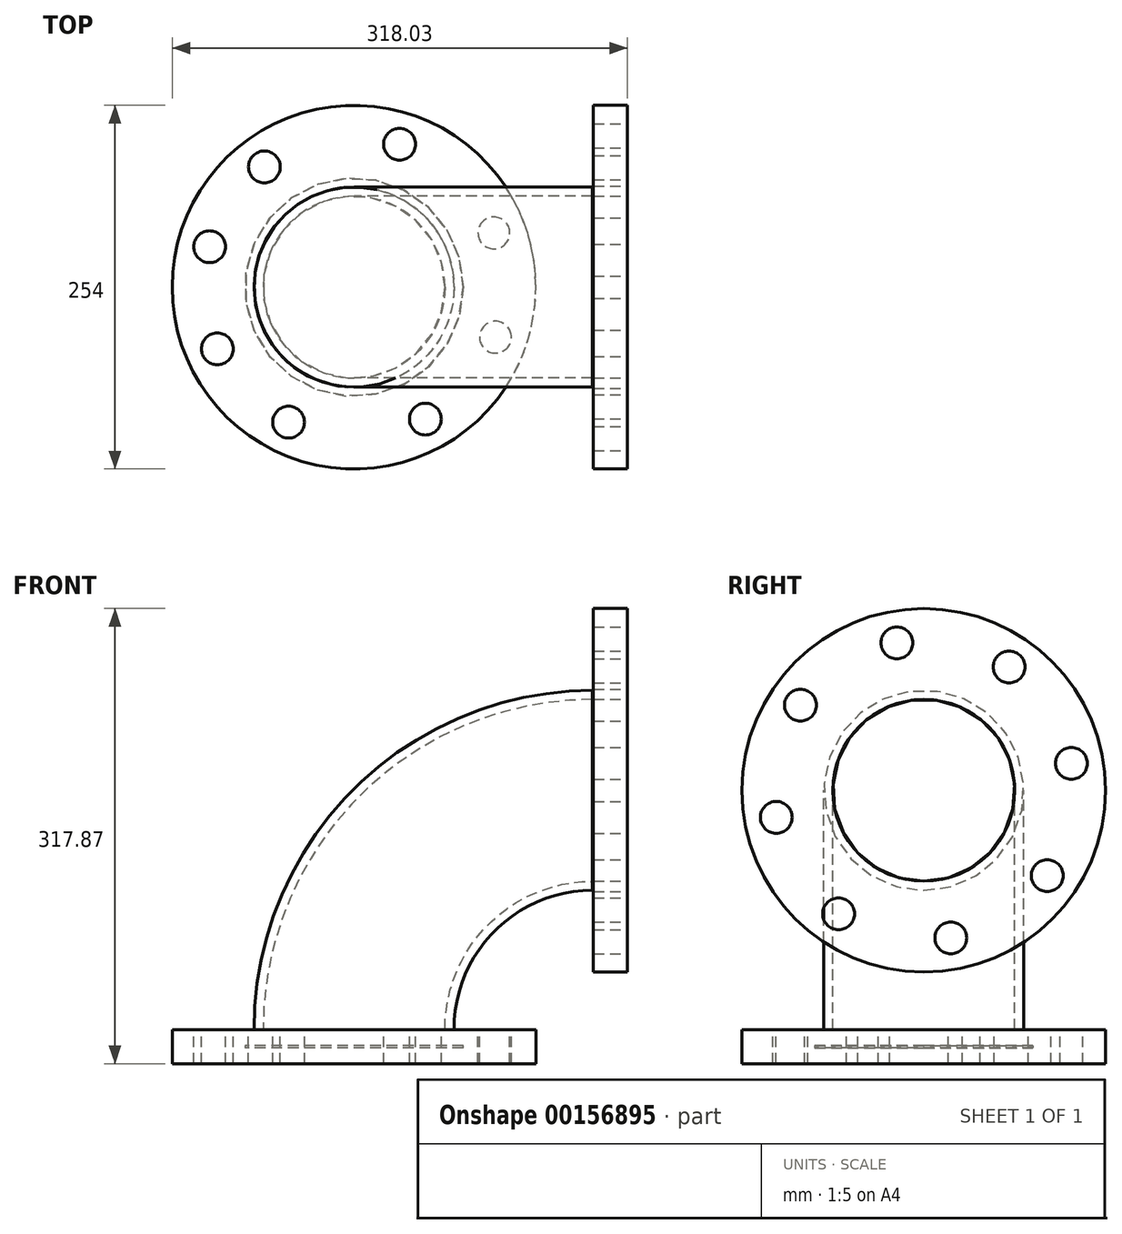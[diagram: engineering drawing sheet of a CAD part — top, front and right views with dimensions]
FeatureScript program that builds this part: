
annotation { "Feature Type Name" : "Feature", "Feature Type Description" : "" }
export const myFeature = defineFeature(function(context is Context, id is Id, definition is map)
    precondition{}
    {
        {
            var Q0;
            Q0=qCreatedBy(makeId("Front.planeOp"),FACE);
            var sketch = newSketch(context, id + "F0", { "sketchPlane" : qUnion([Q0])});
            skLineSegment(sketch, "E0.bottom", {"start": v(0, 0) * mm, "end": v(127, 0) * mm});
            skLineSegment(sketch, "E0.top", {"start": v(0, 23.81) * mm, "end": v(127, 23.81) * mm});
            skLineSegment(sketch, "E0.left", {"start": v(0, 0) * mm, "end": v(0, 23.81) * mm});
            skLineSegment(sketch, "E0.right", {"start": v(127, 0) * mm, "end": v(127, 23.81) * mm});
            skPoint(sketch, "E1.endSnap0", {"position": v(0, 11.9) * mm});
            skLineSegment(sketch, "E2.bottom", {"start": v(191.03, 190.87) * mm, "end": v(167.22, 190.87) * mm});
            skLineSegment(sketch, "E2.top", {"start": v(191.03, 63.87) * mm, "end": v(167.22, 63.87) * mm});
            skLineSegment(sketch, "E2.left", {"start": v(191.03, 190.87) * mm, "end": v(191.03, 63.87) * mm});
            skLineSegment(sketch, "E2.right", {"start": v(167.22, 190.87) * mm, "end": v(167.22, 63.87) * mm});
            skLineSegment(sketch, "E3", {"start": v(0, 23.81) * mm, "end": v(0, 24.18) * mm});
            skLineSegment(sketch, "E4", {"start": v(166.69, 190.87) * mm, "end": v(167.22, 190.87) * mm});
            skPoint(sketch, "E5.visualSharp", {"position": v(0, 190.87) * mm});
            skArc(sketch, "E5.filletArc", {"start": v(166.69, 190.87) * mm, "mid": v(48.82, 142.05) * mm, "end": v(0, 24.18) * mm, "construction": true});
            skLineSegment(sketch, "E6", {"start": v(0, 0) * mm, "end": v(0, 24.18) * mm, "construction": true});
            skLineSegment(sketch, "E7", {"start": v(191.03, 190.87) * mm, "end": v(167.22, 190.87) * mm, "construction": true});
            skLineSegment(sketch, "E8", {"start": v(0, 24.18) * mm, "end": v(63.5, 23.81) * mm});
            skLineSegment(sketch, "E9", {"start": v(167.22, 190.87) * mm, "end": v(167.22, 127.37) * mm});
            skLineSegment(sketch, "E10", {"start": v(63.5, 23.81) * mm, "end": v(63.5, 24.18) * mm});
            skLineSegment(sketch, "E11", {"start": v(166.69, 127.37) * mm, "end": v(167.22, 127.37) * mm});
            skPoint(sketch, "E12.visualSharp", {"position": v(63.5, 127.37) * mm});
            skArc(sketch, "E12.filletArc", {"start": v(166.69, 127.37) * mm, "mid": v(93.72, 97.15) * mm, "end": v(63.5, 24.18) * mm});
            skLineSegment(sketch, "E13", {"start": v(0, 24.18) * mm, "end": v(0, 24.18) * mm});
            skLineSegment(sketch, "E14", {"start": v(167.22, 190.87) * mm, "end": v(166.69, 190.87) * mm});
            skArc(sketch, "E15.filletArc", {"start": v(166.69, 190.87) * mm, "mid": v(48.82, 142.05) * mm, "end": v(0, 24.18) * mm});
            skLineSegment(sketch, "E16", {"start": v(0, -20.98) * mm, "end": v(0, 78.24) * mm, "construction": true});
            skLineSegment(sketch, "E17", {"start": v(208.52, 190.87) * mm, "end": v(129.26, 190.87) * mm, "construction": true});
            skSolve(sketch);
        }
        {
            var Q0;
            Q0=makeQuery(id+"F0.imprint","IMPRINT",FACE,{"disambiguationData":[TD([[makeQuery(id+"F0.imprint","IMPRINT",EDGE,{"derivedFrom":sQuery(id+"F0.wireOp",EDGE,"E2.bottom")}),1.0]])]});
            var Q1;
            Q1=sQuery(id+"F0.wireOp",EDGE,"E17");
            revolve(context, id + "F1", {"entities" : qUnion([Q0]), "axis" : qUnion([Q1]), "revolveType" : RevolveType.FULL});
        }
        {
            var Q0;
            Q0=makeQuery(id+"F0.imprint","IMPRINT",FACE,{"disambiguationData":[TD([[makeQuery(id+"F0.imprint","IMPRINT",EDGE,{"derivedFrom":sQuery(id+"F0.wireOp",EDGE,"E0.bottom")}),1.0]])]});
            var Q1;
            Q1=sQuery(id+"F0.wireOp",EDGE,"E16");
            revolve(context, id + "F2", {"entities" : qUnion([Q0]), "axis" : qUnion([Q1]), "revolveType" : RevolveType.FULL});
        }
        {
            var Q0;
            Q0=makeQuery(id+"F2.opRevolve","SWEPT_FACE",FACE,{"disambiguationData":[OSD([sQuery(id+"F0.wireOp",EDGE,"E0.top")])]});
            var sketch = newSketch(context, id + "F3", { "sketchPlane" : qUnion([Q0])});
            skCircle(sketch, "E18", {"center": v(0, 0) * mm, "radius": 63.5 * mm});
            skCircle(sketch, "E19", {"center": v(0, 0) * mm, "radius": 69.85 * mm});
            skCircle(sketch, "E20", {"center": v(0, 0) * mm, "radius": 104.78 * mm});
            skCircle(sketch, "E21", {"center": v(-95.5, -43.1) * mm, "radius": 11.11 * mm});
            skCircle(sketch, "E22", {"center": v(-45.7, -94.28) * mm, "radius": 11.11 * mm});
            skCircle(sketch, "E23", {"center": v(-100.9, 28.26) * mm, "radius": 11.11 * mm});
            skCircle(sketch, "E24", {"center": v(-62.62, 84) * mm, "radius": 11.11 * mm});
            skCircle(sketch, "E25", {"center": v(31.8, 99.84) * mm, "radius": 11.11 * mm});
            skCircle(sketch, "E26", {"center": v(97.7, 37.87) * mm, "radius": 11.11 * mm});
            skCircle(sketch, "E27", {"center": v(98.79, -34.91) * mm, "radius": 11.11 * mm});
            skCircle(sketch, "E28", {"center": v(49.84, -92.16) * mm, "radius": 11.11 * mm});
            skSolve(sketch);
        }
        {
            var Q0;
            Q0=makeQuery(id+"F3.imprint","IMPRINT",FACE,{"disambiguationData":[TD([[makeQuery(id+"F3.imprint","IMPRINT",EDGE,{"derivedFrom":sQuery(id+"F3.wireOp",EDGE,"E18")}),-1.0]])]});
            var Q1;
            Q1=sQuery(id+"F0.wireOp",EDGE,"E15.filletArc");
            sweep(context, id + "F4", {"operationType" : NewBodyOperationType.ADD, "profiles" : qUnion([Q0]), "path" : qUnion([Q1])});
        }
        {
            var Q0;
            Q0=sQuery(id+"F3.wireOp",VERTEX,"E21.center");
            var Q1;
            Q1=makeQuery(id+"F2.opRevolve","SWEPT_BODY",BODY,{"disambiguationData":[OSD([sQuery(id+"F0.wireOp",EDGE,"E0.bottom"),sQuery(id+"F0.wireOp",EDGE,"E0.top"),sQuery(id+"F0.wireOp",EDGE,"E0.left"),sQuery(id+"F0.wireOp",EDGE,"E0.right")])]});
            hole(context, id + "F5", {"style" : HoleStyle.SIMPLE, "endStyle" : HoleEndStyle.THROUGH, "holeDiameter" : 22.22 * mm, "locations" : qUnion([Q0]), "scope" : qUnion([Q1]), "isTappedThrough" : true});
        }
        {
            var Q0;
            Q0=sQuery(id+"F3.wireOp",VERTEX,"E22.center");
            var Q1;
            Q1=makeQuery(id+"F2.opRevolve","SWEPT_BODY",BODY,{"disambiguationData":[OSD([sQuery(id+"F0.wireOp",EDGE,"E0.bottom"),sQuery(id+"F0.wireOp",EDGE,"E0.top"),sQuery(id+"F0.wireOp",EDGE,"E0.left"),sQuery(id+"F0.wireOp",EDGE,"E0.right")])]});
            hole(context, id + "F6", {"style" : HoleStyle.SIMPLE, "endStyle" : HoleEndStyle.THROUGH, "holeDiameter" : 22.22 * mm, "locations" : qUnion([Q0]), "scope" : qUnion([Q1]), "isTappedThrough" : true});
        }
        {
            var Q0;
            Q0=sQuery(id+"F3.wireOp",VERTEX,"E23.center");
            var Q1;
            Q1=makeQuery(id+"F2.opRevolve","SWEPT_BODY",BODY,{"disambiguationData":[OSD([sQuery(id+"F0.wireOp",EDGE,"E0.bottom"),sQuery(id+"F0.wireOp",EDGE,"E0.top"),sQuery(id+"F0.wireOp",EDGE,"E0.left"),sQuery(id+"F0.wireOp",EDGE,"E0.right")])]});
            hole(context, id + "F7", {"style" : HoleStyle.SIMPLE, "endStyle" : HoleEndStyle.THROUGH, "holeDiameter" : 22.22 * mm, "locations" : qUnion([Q0]), "scope" : qUnion([Q1]), "isTappedThrough" : true});
        }
        {
            var Q0;
            Q0=sQuery(id+"F3.wireOp",VERTEX,"E24.center");
            var Q1;
            Q1=sQuery(id+"F3.wireOp",VERTEX,"E25.center");
            var Q2;
            Q2=sQuery(id+"F3.wireOp",VERTEX,"E26.center");
            var Q3;
            Q3=sQuery(id+"F3.wireOp",VERTEX,"E27.center");
            var Q4;
            Q4=sQuery(id+"F3.wireOp",VERTEX,"E28.center");
            var Q5;
            Q5=makeQuery(id+"F2.opRevolve","SWEPT_BODY",BODY,{"disambiguationData":[OSD([sQuery(id+"F0.wireOp",EDGE,"E0.bottom"),sQuery(id+"F0.wireOp",EDGE,"E0.top"),sQuery(id+"F0.wireOp",EDGE,"E0.left"),sQuery(id+"F0.wireOp",EDGE,"E0.right")])]});
            hole(context, id + "F8", {"style" : HoleStyle.SIMPLE, "endStyle" : HoleEndStyle.THROUGH, "holeDiameter" : 22.22 * mm, "locations" : qUnion([Q0, Q1, Q2, Q3, Q4]), "scope" : qUnion([Q5]), "isTappedThrough" : true});
        }
        {
            var Q0;
            Q0=makeQuery(id+"F1.opRevolve","SWEPT_FACE",FACE,{"disambiguationData":[OSD([sQuery(id+"F0.wireOp",EDGE,"E2.left")])]});
            var sketch = newSketch(context, id + "F9", { "sketchPlane" : qUnion([Q0])});
            skCircle(sketch, "E29", {"center": v(0, 190.87) * mm, "radius": 104.77 * mm, "construction": true});
            skCircle(sketch, "E30", {"center": v(-59.55, 104.66) * mm, "radius": 11.11 * mm});
            skLineSegment(sketch, "E31.anchor1", {"start": v(0, 190.87) * mm, "end": v(-59.55, 104.66) * mm, "construction": true});
            skLineSegment(sketch, "E31.anchor2", {"start": v(0, 190.87) * mm, "end": v(-59.55, 104.66) * mm, "construction": true});
            skCircle(sketch, "E32.1.0", {"center": v(18.85, 87.8) * mm, "radius": 11.11 * mm});
            skCircle(sketch, "E32.2.0", {"center": v(86.2, 131.32) * mm, "radius": 11.11 * mm});
            skCircle(sketch, "E33.1.3.0", {"center": v(103.07, 209.72) * mm, "radius": 11.11 * mm});
            skCircle(sketch, "E33.1.4.0", {"center": v(59.55, 277.08) * mm, "radius": 11.11 * mm});
            skCircle(sketch, "E33.1.5.0", {"center": v(-18.85, 293.93) * mm, "radius": 11.11 * mm});
            skCircle(sketch, "E33.1.6.0", {"center": v(-86.2, 250.42) * mm, "radius": 11.11 * mm});
            skCircle(sketch, "E33.1.7.0", {"center": v(-103.07, 172.02) * mm, "radius": 11.11 * mm});
            skSolve(sketch);
        }
        {
            var Q0;
            Q0=sQuery(id+"F9.wireOp",VERTEX,"E31.anchor1.end");
            var Q1;
            Q1=sQuery(id+"F9.wireOp",VERTEX,"E33.1.7.0.center");
            var Q2;
            Q2=sQuery(id+"F9.wireOp",VERTEX,"E33.1.6.0.center");
            var Q3;
            Q3=sQuery(id+"F9.wireOp",VERTEX,"E33.1.5.0.center");
            var Q4;
            Q4=sQuery(id+"F9.wireOp",VERTEX,"E33.1.4.0.center");
            var Q5;
            Q5=sQuery(id+"F9.wireOp",VERTEX,"E33.1.3.0.center");
            var Q6;
            Q6=sQuery(id+"F9.wireOp",VERTEX,"E32.2.0.center");
            var Q7;
            Q7=sQuery(id+"F9.wireOp",VERTEX,"E32.1.0.center");
            var Q8;
            Q8=makeQuery(id+"F1.opRevolve","SWEPT_BODY",BODY,{"disambiguationData":[OSD([sQuery(id+"F0.wireOp",EDGE,"E2.bottom"),sQuery(id+"F0.wireOp",EDGE,"E2.top"),sQuery(id+"F0.wireOp",EDGE,"E2.left"),sQuery(id+"F0.wireOp",EDGE,"E2.right"),sQuery(id+"F0.wireOp",EDGE,"E9")])]});
            hole(context, id + "F10", {"style" : HoleStyle.SIMPLE, "endStyle" : HoleEndStyle.THROUGH, "holeDiameter" : 22.22 * mm, "locations" : qUnion([Q0, Q1, Q2, Q3, Q4, Q5, Q6, Q7]), "scope" : qUnion([Q8]), "isTappedThrough" : true});
        }
        {
            var Q0;
            Q0=sQuery(id+"F9.wireOp",VERTEX,"E29.center");
            var Q1;
            Q1=makeQuery(id+"F1.opRevolve","SWEPT_BODY",BODY,{"disambiguationData":[OSD([sQuery(id+"F0.wireOp",EDGE,"E2.bottom"),sQuery(id+"F0.wireOp",EDGE,"E2.top"),sQuery(id+"F0.wireOp",EDGE,"E2.left"),sQuery(id+"F0.wireOp",EDGE,"E2.right"),sQuery(id+"F0.wireOp",EDGE,"E9")])]});
            hole(context, id + "F11", {"style" : HoleStyle.SIMPLE, "endStyle" : HoleEndStyle.THROUGH, "holeDiameter" : 127 * mm, "locations" : qUnion([Q0]), "scope" : qUnion([Q1]), "isTappedThrough" : true});
        }
        {
            var Q0;
            Q0=makeQuery(id+"F4.opSweep","SWEPT_FACE",FACE,{"disambiguationData":[OSD([sQuery(id+"F0.wireOp",EDGE,"E15.filletArc"),sQuery(id+"F3.wireOp",EDGE,"E19")])]});
            shell(context, id + "F12", {"entities" : qUnion([Q0]), "thickness" : 12.7 * mm});
        }
    });
